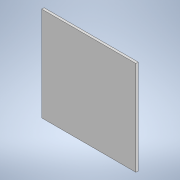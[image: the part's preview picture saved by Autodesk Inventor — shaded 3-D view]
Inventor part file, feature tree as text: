
AUTODESK INVENTOR PART (.ipt)
format: ipt  version: 2020 (Build 240168000, 168)  size: 87,552 bytes
history: native  units: in
note: dims shown in document units (in); Inventor stores cm internally (conversion verified against a paired STEP export)
features: extrude x1, sketch x1
ambient origin geometry x8: Origin, YZ Plane, XZ Plane, XY Plane, X Axis, Y Axis, Z Axis, Center Point
bodies: Solid1 (feature_tree)
feature tree (2):
  extrude  "Extrusion1"  Depth=4.0in
  sketch  "Sketch1"  dims[d0=4.0in d1=4.0in d2=0.1in d3=0.0in]
